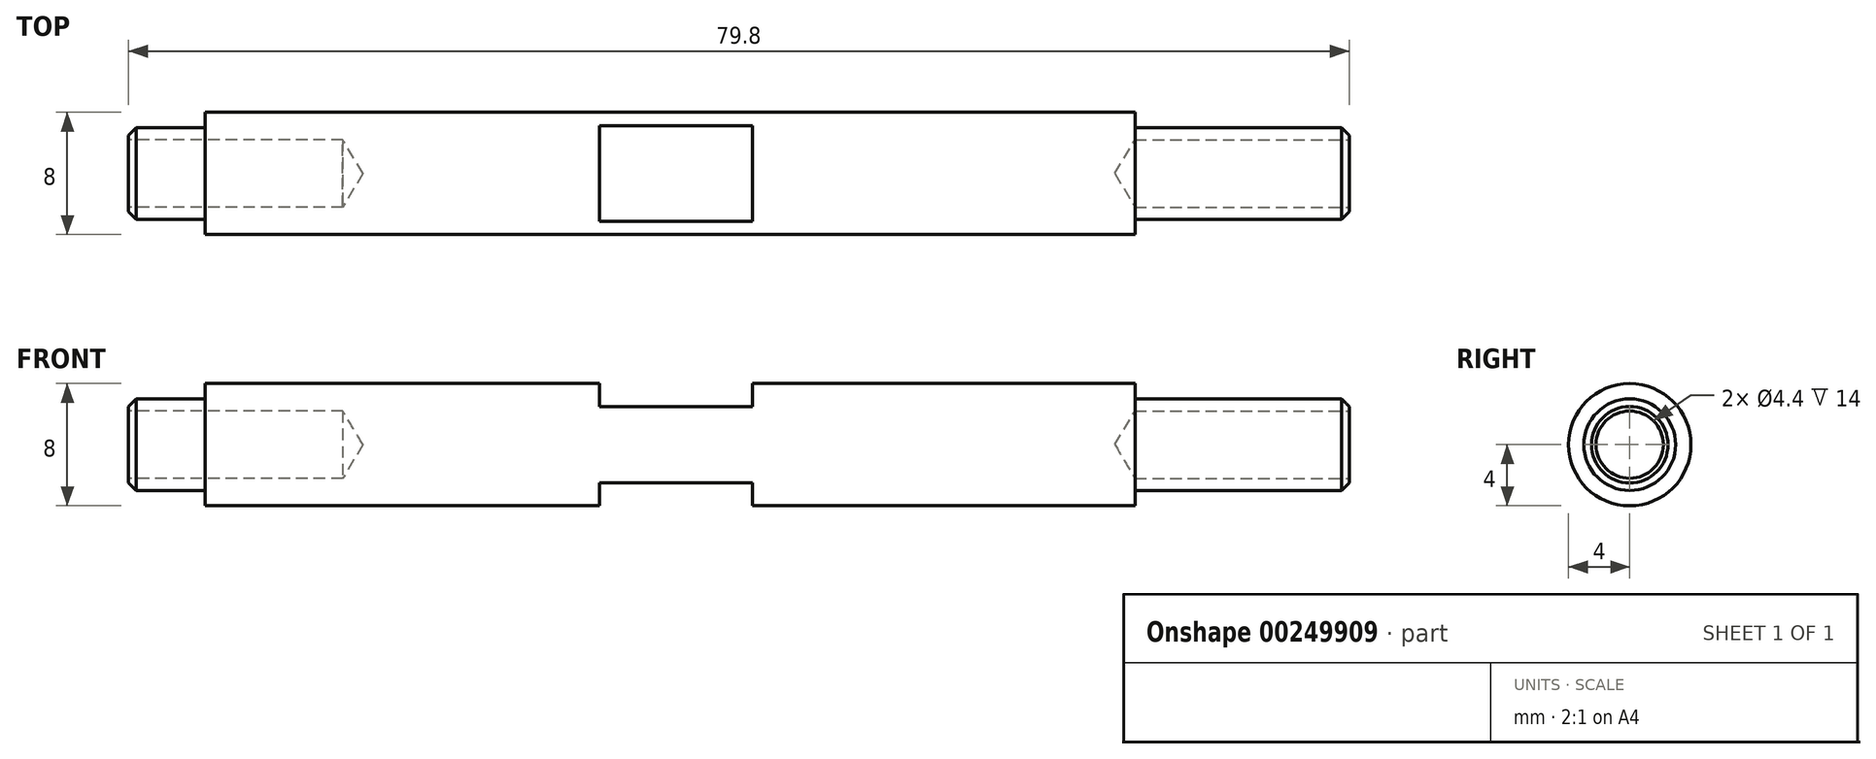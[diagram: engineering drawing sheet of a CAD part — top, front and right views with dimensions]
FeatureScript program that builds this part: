
annotation { "Feature Type Name" : "Feature", "Feature Type Description" : "" }
export const myFeature = defineFeature(function(context is Context, id is Id, definition is map)
    precondition{}
    {
        {
            var Q0;
            Q0=qCreatedBy(makeId("Front.planeOp"),FACE);
            var sketch = newSketch(context, id + "F0", { "sketchPlane" : qUnion([Q0])});
            skLineSegment(sketch, "E0", {"start": v(0, 0) * mm, "end": v(0, 4) * mm});
            skLineSegment(sketch, "E1", {"start": v(60.8, 4) * mm, "end": v(60.8, 0) * mm});
            skLineSegment(sketch, "E2", {"start": v(60.8, 0) * mm, "end": v(0, 0) * mm});
            skLineSegment(sketch, "E3", {"start": v(0, 0) * mm, "end": v(-5, 0) * mm});
            skLineSegment(sketch, "E4", {"start": v(-5, 0) * mm, "end": v(-5, 3) * mm});
            skLineSegment(sketch, "E5", {"start": v(-5, 3) * mm, "end": v(0, 3) * mm});
            skLineSegment(sketch, "E6", {"start": v(60.8, 3) * mm, "end": v(74.8, 3) * mm});
            skLineSegment(sketch, "E7", {"start": v(74.8, 3) * mm, "end": v(74.8, 0) * mm});
            skLineSegment(sketch, "E8", {"start": v(74.8, 0) * mm, "end": v(60.8, 0) * mm});
            skLineSegment(sketch, "E9", {"start": v(0, 4) * mm, "end": v(60.8, 4) * mm});
            skSolve(sketch);
        }
        {
            var Q0;
            {var subQ0=sQuery(id+"F0.wireOp",EDGE,"E2");Q0=makeQuery(id+"F0.imprint","IMPRINT",FACE,{"disambiguationData":[TD([[makeQuery(id+"F0.imprint","IMPRINT",EDGE,{"derivedFrom":subQ0}),-1.0]])]});}
            var Q1;
            {var subQ0=sQuery(id+"F0.wireOp",EDGE,"E3");Q1=makeQuery(id+"F0.imprint","IMPRINT",FACE,{"disambiguationData":[TD([[makeQuery(id+"F0.imprint","IMPRINT",EDGE,{"derivedFrom":subQ0}),-1.0]])]});}
            var Q2;
            {var subQ2=sQuery(id+"F0.wireOp",EDGE,"E6");Q2=makeQuery(id+"F0.imprint","IMPRINT",FACE,{"disambiguationData":[TD([[makeQuery(id+"F0.imprint","IMPRINT",EDGE,{"derivedFrom":subQ2}),-1.0]])]});}
            var Q3;
            Q3=sQuery(id+"F0.wireOp",EDGE,"E2");
            revolve(context, id + "F1", {"entities" : qUnion([Q0, Q1, Q2]), "axis" : qUnion([Q3]), "revolveType" : RevolveType.FULL});
        }
        {
            var Q0;
            Q0=qCreatedBy(makeId("Front.planeOp"),FACE);
            var sketch = newSketch(context, id + "F2", { "sketchPlane" : qUnion([Q0])});
            skLineSegment(sketch, "E10", {"start": v(25.8, 4) * mm, "end": v(35.8, 4) * mm});
            skLineSegment(sketch, "E11", {"start": v(35.8, -4) * mm, "end": v(25.8, -4) * mm});
            skLineSegment(sketch, "E12", {"start": v(25.8, 2.5) * mm, "end": v(35.8, 2.5) * mm});
            skLineSegment(sketch, "E13", {"start": v(35.8, 4) * mm, "end": v(35.8, 2.5) * mm});
            skLineSegment(sketch, "E14", {"start": v(25.8, 2.5) * mm, "end": v(25.8, 4) * mm});
            skLineSegment(sketch, "E15.MirrorCS", {"start": v(25.8, -2.5) * mm, "end": v(35.8, -2.5) * mm});
            skLineSegment(sketch, "E16.MirrorCS", {"start": v(35.8, -4) * mm, "end": v(35.8, -2.5) * mm});
            skLineSegment(sketch, "E17.MirrorCS", {"start": v(25.8, -2.5) * mm, "end": v(25.8, -4) * mm});
            skLineSegment(sketch, "E18.MirrorCS", {"start": v(0, -4) * mm, "end": v(60.8, -4) * mm});
            skPoint(sketch, "E19.orphan", {"position": v(0, 4) * mm});
            skPoint(sketch, "E20.orphan", {"position": v(60.8, 4) * mm});
            skSolve(sketch);
        }
        {
            var Q0;
            Q0 = qSketchRegion(id + "F2", true);
            extrude(context, id + "F3", {"entities" : qUnion([Q0]), "operationType" : NewBodyOperationType.REMOVE, "endBound" : BoundingType.SYMMETRIC, "oppositeDirection" : true, "depth" : 25 * mm});
        }
        {
            var Q0;
            Q0=makeQuery(id+"F1.opRevolve","SWEPT_FACE",FACE,{"disambiguationData":[OSD([sQuery(id+"F0.wireOp",EDGE,"E7")])]});
            var sketch = newSketch(context, id + "F4", { "sketchPlane" : qUnion([Q0])});
            skPoint(sketch, "E21", {"position": v(0, 0) * mm});
            skSolve(sketch);
        }
        {
            var Q0;
            Q0=sQuery(id+"F4.wireOp",VERTEX,"E21");
            var Q1;
            Q1=makeQuery(id+"F1.opRevolve","SWEPT_BODY",BODY,{"disambiguationData":[OSD([sQuery(id+"F0.wireOp",EDGE,"E0"),sQuery(id+"F0.wireOp",EDGE,"E1"),sQuery(id+"F0.wireOp",EDGE,"E2"),sQuery(id+"F0.wireOp",EDGE,"E3"),sQuery(id+"F0.wireOp",EDGE,"E4"),sQuery(id+"F0.wireOp",EDGE,"E5"),sQuery(id+"F0.wireOp",EDGE,"E6"),sQuery(id+"F0.wireOp",EDGE,"E7"),sQuery(id+"F0.wireOp",EDGE,"E8"),sQuery(id+"F0.wireOp",EDGE,"E9")])]});
            hole(context, id + "F5", {"style" : HoleStyle.SIMPLE, "endStyle" : HoleEndStyle.BLIND, "standardTappedOrClearance" : lookupTablePath({ "standard" : "ISO", "fit" : "Normal", "size" : "M4", "type" : "Clearance" }), "standardBlindInLast" : lookupTablePath({ "fit" : "Standard", "standard" : "ISO", "size" : "M4", "type" : "Clearance" }), "holeDiameter" : 4.4 * mm, "holeDepth" : 14 * mm, "tappedDepth" : 12 * mm, "tapClearance" : 3, "locations" : qUnion([Q0]), "scope" : qUnion([Q1])});
        }
        {
            var Q0;
            Q0=makeQuery(id+"F1.opRevolve","SWEPT_FACE",FACE,{"disambiguationData":[OSD([sQuery(id+"F0.wireOp",EDGE,"E4")])]});
            var sketch = newSketch(context, id + "F6", { "sketchPlane" : qUnion([Q0])});
            skPoint(sketch, "E22", {"position": v(0, 0) * mm});
            skSolve(sketch);
        }
        {
            var Q0;
            Q0=sQuery(id+"F6.wireOp",VERTEX,"E22");
            var Q1;
            Q1=makeQuery(id+"F1.opRevolve","SWEPT_BODY",BODY,{"disambiguationData":[OSD([sQuery(id+"F0.wireOp",EDGE,"E0"),sQuery(id+"F0.wireOp",EDGE,"E1"),sQuery(id+"F0.wireOp",EDGE,"E2"),sQuery(id+"F0.wireOp",EDGE,"E3"),sQuery(id+"F0.wireOp",EDGE,"E4"),sQuery(id+"F0.wireOp",EDGE,"E5"),sQuery(id+"F0.wireOp",EDGE,"E6"),sQuery(id+"F0.wireOp",EDGE,"E7"),sQuery(id+"F0.wireOp",EDGE,"E8"),sQuery(id+"F0.wireOp",EDGE,"E9")])]});
            hole(context, id + "F7", {"style" : HoleStyle.SIMPLE, "endStyle" : HoleEndStyle.BLIND, "standardTappedOrClearance" : lookupTablePath({ "standard" : "ISO", "fit" : "Normal", "size" : "M4", "type" : "Clearance" }), "standardBlindInLast" : lookupTablePath({ "fit" : "Standard", "standard" : "ISO", "size" : "M4", "type" : "Clearance" }), "holeDiameter" : 4.4 * mm, "holeDepth" : 14 * mm, "tappedDepth" : 12 * mm, "tapClearance" : 3, "locations" : qUnion([Q0]), "scope" : qUnion([Q1])});
        }
        {
            var Q0;
            Q0=makeQuery(id+"F1.opRevolve","SWEPT_EDGE",EDGE,{"disambiguationData":[OSD([sQuery(id+"F0.wireOp",EDGE,"E4"),sQuery(id+"F0.wireOp",EDGE,"E5")])]});
            var Q1;
            Q1=makeQuery(id+"F1.opRevolve","SWEPT_EDGE",EDGE,{"disambiguationData":[OSD([sQuery(id+"F0.wireOp",EDGE,"E6"),sQuery(id+"F0.wireOp",EDGE,"E7")])]});
            chamfer(context, id + "F8", {"entities" : qUnion([Q0, Q1]), "width" : .5 * mm, "tangentPropagation" : true});
        }
    });
